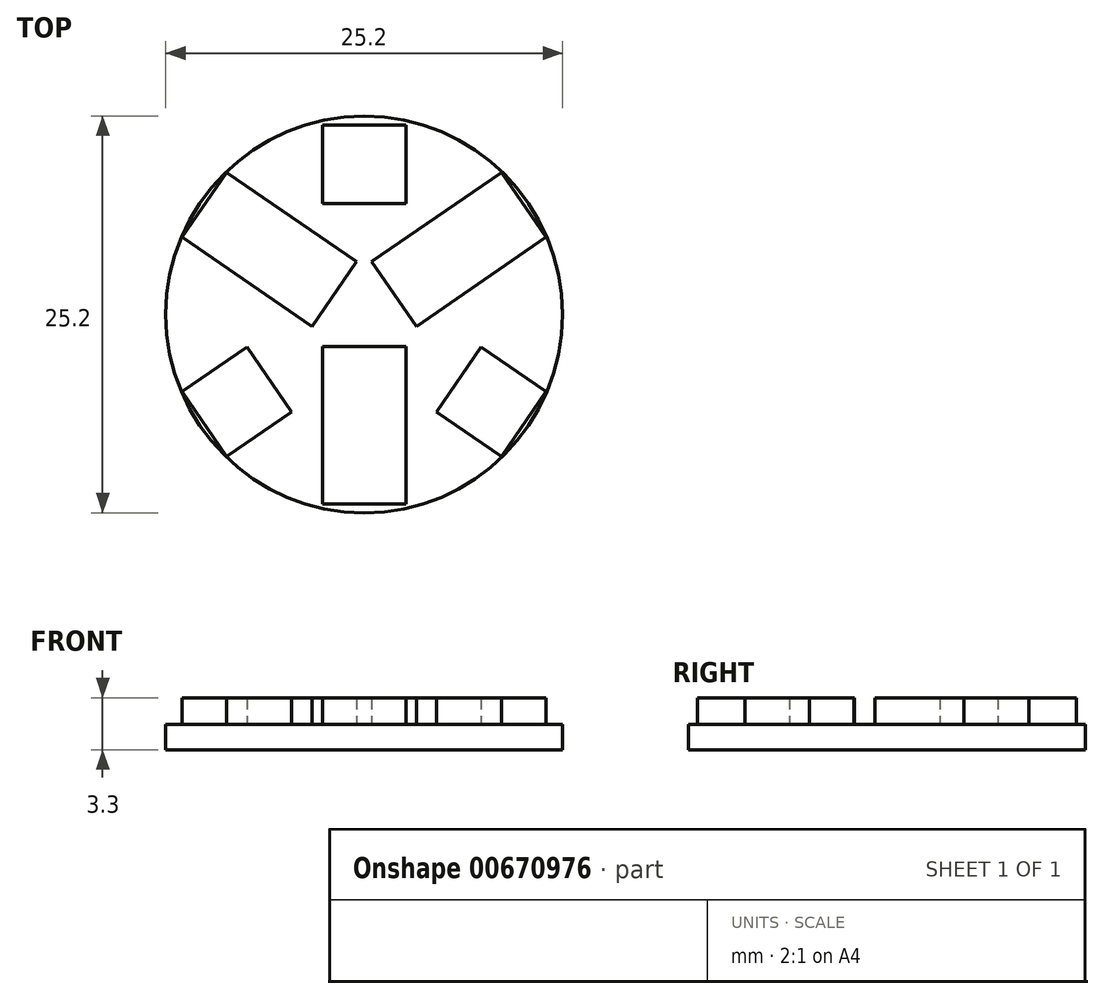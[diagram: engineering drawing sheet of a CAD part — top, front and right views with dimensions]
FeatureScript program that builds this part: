
annotation { "Feature Type Name" : "Feature", "Feature Type Description" : "" }
export const myFeature = defineFeature(function(context is Context, id is Id, definition is map)
    precondition{}
    {
        {
            var Q0;
            Q0=qCreatedBy(makeId("Top.planeOp"),FACE);
            var sketch = newSketch(context, id + "F0", { "sketchPlane" : qUnion([Q0])});
            skCircle(sketch, "E0", {"center": v(0, 0) * mm, "radius": 12.6 * mm});
            skSolve(sketch);
        }
        {
            var Q0;
            Q0=makeQuery(id+"F0.imprint","IMPRINT",FACE,{"disambiguationData":[TD([[makeQuery(id+"F0.imprint","IMPRINT",EDGE,{"derivedFrom":sQuery(id+"F0.wireOp",EDGE,"E0")}),1.0]])]});
            extrude(context, id + "F1", {"entities" : qUnion([Q0]), "depth" : 1.6 * mm, "offsetDistance" : 25 * mm});
        }
        {
            var Q0;
            Q0=makeQuery(id+"F1.opExtrude","CAP_FACE",FACE,{"disambiguationData":[OSD([sQuery(id+"F0.wireOp",EDGE,"E0")])],"isStart":false});
            var sketch = newSketch(context, id + "F2", { "sketchPlane" : qUnion([Q0])});
            skLineSegment(sketch, "E1", {"start": v(0, -12.6) * mm, "end": v(0, 12.6) * mm, "construction": true});
            skLineSegment(sketch, "E2", {"start": v(-12.6, 0) * mm, "end": v(12.6, 0) * mm, "construction": true});
            skPoint(sketch, "E2.endSnap0", {"position": v(0, 0) * mm});
            skLineSegment(sketch, "E3.bottom", {"start": v(0, -12.04) * mm, "end": v(2.65, -12.04) * mm});
            skLineSegment(sketch, "E3.top", {"start": v(0, -7.04) * mm, "end": v(2.65, -7.04) * mm});
            skLineSegment(sketch, "E3.left", {"start": v(0, -12.04) * mm, "end": v(0, -7.04) * mm});
            skLineSegment(sketch, "E3.right", {"start": v(2.65, -12.04) * mm, "end": v(2.65, -7.04) * mm});
            skLineSegment(sketch, "E4", {"start": v(0, -12.6) * mm, "end": v(0, -12.04) * mm, "construction": true});
            skLineSegment(sketch, "E5.MirrorCS", {"start": v(0, -7.04) * mm, "end": v(-2.65, -7.04) * mm});
            skLineSegment(sketch, "E6.MirrorCS", {"start": v(-2.65, -12.04) * mm, "end": v(-2.65, -7.04) * mm});
            skLineSegment(sketch, "E7.MirrorCS", {"start": v(0, -12.04) * mm, "end": v(-2.65, -12.04) * mm});
            skLineSegment(sketch, "E8.MirrorCS", {"start": v(0, -2.04) * mm, "end": v(-2.65, -2.04) * mm});
            skLineSegment(sketch, "E9.MirrorCS", {"start": v(-2.65, -2.04) * mm, "end": v(-2.65, -7.04) * mm});
            skLineSegment(sketch, "E10.MirrorCS", {"start": v(2.65, -2.04) * mm, "end": v(2.65, -7.04) * mm});
            skLineSegment(sketch, "E11.MirrorCS", {"start": v(0, -2.04) * mm, "end": v(2.65, -2.04) * mm});
            skLineSegment(sketch, "E12", {"start": v(0, 0) * mm, "end": v(8.6, -9.22) * mm, "construction": true});
            skLineSegment(sketch, "E13", {"start": v(0, 0) * mm, "end": v(11.68, -4.72) * mm, "construction": true});
            skLineSegment(sketch, "E14", {"start": v(8.6, -9.22) * mm, "end": v(10.14, -6.97) * mm, "construction": true});
            skLineSegment(sketch, "E15.bottom", {"start": v(8.72, -9.03) * mm, "end": v(4.6, -6.2) * mm});
            skLineSegment(sketch, "E15.top", {"start": v(11.55, -4.9) * mm, "end": v(7.43, -2.08) * mm});
            skLineSegment(sketch, "E15.left", {"start": v(8.72, -9.03) * mm, "end": v(10.14, -6.97) * mm});
            skLineSegment(sketch, "E15.right", {"start": v(4.6, -6.2) * mm, "end": v(7.43, -2.08) * mm});
            skLineSegment(sketch, "E16", {"start": v(10.14, -6.97) * mm, "end": v(11.68, -4.72) * mm, "construction": true});
            skLineSegment(sketch, "E17", {"start": v(10.14, -6.97) * mm, "end": v(11.55, -4.9) * mm});
            skLineSegment(sketch, "E18.MirrorCS", {"start": v(-4.6, -6.2) * mm, "end": v(-7.43, -2.08) * mm});
            skLineSegment(sketch, "E19.MirrorCS", {"start": v(-11.55, -4.9) * mm, "end": v(-7.43, -2.08) * mm});
            skLineSegment(sketch, "E20.MirrorCS", {"start": v(-10.14, -6.97) * mm, "end": v(-11.68, -4.72) * mm});
            skLineSegment(sketch, "E21.MirrorCS", {"start": v(-8.72, -9.03) * mm, "end": v(-4.6, -6.2) * mm});
            skLineSegment(sketch, "E22.MirrorCS", {"start": v(-8.6, -9.22) * mm, "end": v(-10.14, -6.97) * mm, "construction": true});
            skLineSegment(sketch, "E23.MirrorCS", {"start": v(-10.14, -6.97) * mm, "end": v(-11.68, -4.72) * mm, "construction": true});
            skLineSegment(sketch, "E24.MirrorCS", {"start": v(-8.6, -9.22) * mm, "end": v(-10.14, -6.97) * mm});
            skLineSegment(sketch, "E25.MirrorCS", {"start": v(-2.65, 12.04) * mm, "end": v(-2.65, 7.04) * mm});
            skLineSegment(sketch, "E26.MirrorCS", {"start": v(0, 12.04) * mm, "end": v(-2.65, 12.04) * mm});
            skLineSegment(sketch, "E27.MirrorCS", {"start": v(2.65, 12.04) * mm, "end": v(2.65, 7.04) * mm});
            skLineSegment(sketch, "E28.MirrorCS", {"start": v(0, 12.04) * mm, "end": v(2.65, 12.04) * mm});
            skLineSegment(sketch, "E29.MirrorCS", {"start": v(0, 7.04) * mm, "end": v(2.65, 7.04) * mm});
            skLineSegment(sketch, "E30.MirrorCS", {"start": v(0, 7.04) * mm, "end": v(-2.65, 7.04) * mm});
            skLineSegment(sketch, "E31.MirrorCS", {"start": v(11.55, 4.9) * mm, "end": v(7.43, 2.08) * mm});
            skLineSegment(sketch, "E32.MirrorCS", {"start": v(4.6, 6.2) * mm, "end": v(7.43, 2.08) * mm});
            skLineSegment(sketch, "E33.MirrorCS", {"start": v(8.72, 9.03) * mm, "end": v(4.6, 6.2) * mm});
            skLineSegment(sketch, "E34.MirrorCS", {"start": v(10.14, 6.97) * mm, "end": v(11.68, 4.72) * mm});
            skLineSegment(sketch, "E35.MirrorCS", {"start": v(8.6, 9.22) * mm, "end": v(10.14, 6.97) * mm});
            skLineSegment(sketch, "E36.MirrorCS", {"start": v(-4.6, 6.2) * mm, "end": v(-7.43, 2.08) * mm});
            skLineSegment(sketch, "E37.MirrorCS", {"start": v(-11.55, 4.9) * mm, "end": v(-7.43, 2.08) * mm});
            skLineSegment(sketch, "E38.MirrorCS", {"start": v(-10.14, 6.97) * mm, "end": v(-11.68, 4.72) * mm});
            skLineSegment(sketch, "E39.MirrorCS", {"start": v(-8.6, 9.22) * mm, "end": v(-10.14, 6.97) * mm});
            skLineSegment(sketch, "E40.MirrorCS", {"start": v(-8.72, 9.03) * mm, "end": v(-4.6, 6.2) * mm});
            skLineSegment(sketch, "E41.MirrorCS", {"start": v(-0.48, 3.36) * mm, "end": v(-4.6, 6.2) * mm});
            skLineSegment(sketch, "E42.MirrorCS", {"start": v(-3.31, -0.76) * mm, "end": v(-7.43, 2.08) * mm});
            skLineSegment(sketch, "E43.MirrorCS", {"start": v(-1.9, 1.3) * mm, "end": v(-3.44, -0.94) * mm});
            skLineSegment(sketch, "E44.MirrorCS", {"start": v(-0.35, 3.55) * mm, "end": v(-1.9, 1.3) * mm});
            skLineSegment(sketch, "E45.MirrorCS", {"start": v(3.31, -0.76) * mm, "end": v(7.43, 2.08) * mm});
            skLineSegment(sketch, "E46.MirrorCS", {"start": v(0.48, 3.36) * mm, "end": v(4.6, 6.2) * mm});
            skLineSegment(sketch, "E47.MirrorCS", {"start": v(0.35, 3.55) * mm, "end": v(1.9, 1.3) * mm});
            skLineSegment(sketch, "E48.MirrorCS", {"start": v(1.9, 1.3) * mm, "end": v(3.44, -0.94) * mm});
            skSolve(sketch);
        }
        {
            var Q0;
            Q0 = qSketchRegion(id + "F2", true);
            extrude(context, id + "F3", {"entities" : qUnion([Q0]), "operationType" : NewBodyOperationType.ADD, "depth" : 1.7 * mm, "offsetDistance" : 25 * mm});
        }
    });
